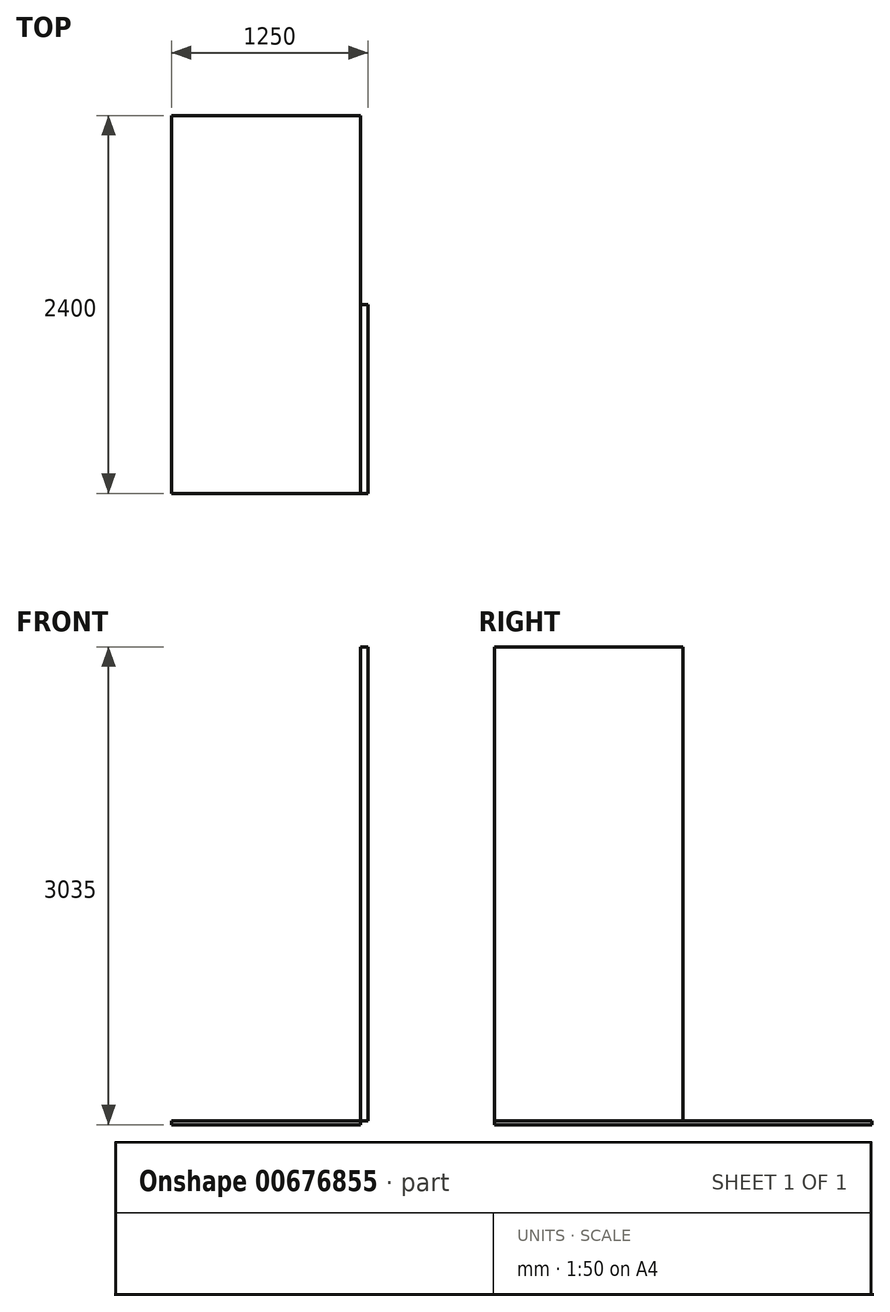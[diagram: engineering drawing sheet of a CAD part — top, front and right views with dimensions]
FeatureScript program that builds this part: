
annotation { "Feature Type Name" : "Feature", "Feature Type Description" : "" }
export const myFeature = defineFeature(function(context is Context, id is Id, definition is map)
    precondition{}
    {
        {
            var Q0;
            Q0=qCreatedBy(makeId("Top.planeOp"),FACE);
            var sketch = newSketch(context, id + "F0", { "sketchPlane" : qUnion([Q0])});
            skLineSegment(sketch, "E0.bottom", {"start": v(600, 1200) * mm, "end": v(-600, 1200) * mm});
            skLineSegment(sketch, "E0.top", {"start": v(600, -1200) * mm, "end": v(-600, -1200) * mm});
            skLineSegment(sketch, "E0.left", {"start": v(600, 1200) * mm, "end": v(600, -1200) * mm});
            skLineSegment(sketch, "E0.right", {"start": v(-600, 1200) * mm, "end": v(-600, -1200) * mm});
            skPoint(sketch, "E0.middle", {"position": v(0, 0) * mm});
            skSolve(sketch);
        }
        {
            var Q0;
            Q0 = qSketchRegion(id + "F0", true);
            extrude(context, id + "F1", {"entities" : qUnion([Q0]), "depth" : 25 * mm, "offsetDistance" : 25 * mm});
        }
        {
            var Q0;
            Q0=makeQuery(id+"F1.opExtrude","SWEPT_FACE",FACE,{"disambiguationData":[OSD([sQuery(id+"F0.wireOp",EDGE,"E0.left")])]});
            var sketch = newSketch(context, id + "F2", { "sketchPlane" : qUnion([Q0])});
            skLineSegment(sketch, "E1.0", {"start": v(1200, 25) * mm, "end": v(-1200, 25) * mm, "construction": true});
            skLineSegment(sketch, "E2.bottom", {"start": v(-1200, 25) * mm, "end": v(0, 25) * mm});
            skLineSegment(sketch, "E2.top", {"start": v(-1200, 3035) * mm, "end": v(0, 3035) * mm});
            skLineSegment(sketch, "E2.left", {"start": v(-1200, 25) * mm, "end": v(-1200, 3035) * mm});
            skLineSegment(sketch, "E2.right", {"start": v(0, 25) * mm, "end": v(0, 3035) * mm});
            skSolve(sketch);
        }
        {
            var Q0;
            Q0 = qSketchRegion(id + "F2", true);
            extrude(context, id + "F3", {"entities" : qUnion([Q0]), "depth" : 50 * mm, "offsetDistance" : 25 * mm});
        }
    });
